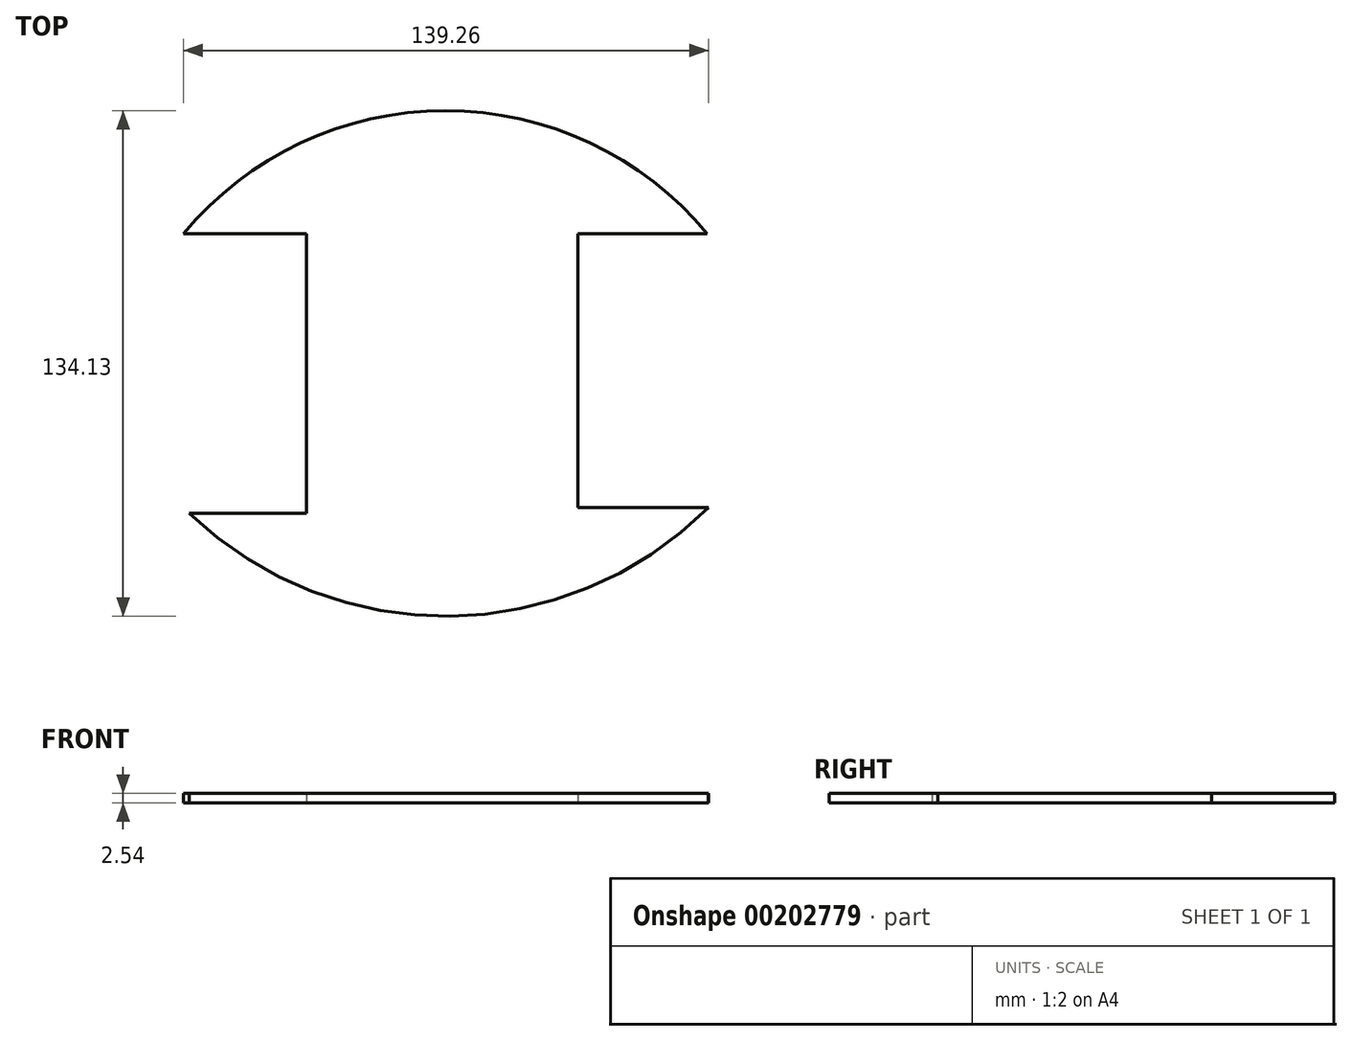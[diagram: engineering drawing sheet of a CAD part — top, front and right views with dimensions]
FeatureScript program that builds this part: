
annotation { "Feature Type Name" : "Feature", "Feature Type Description" : "" }
export const myFeature = defineFeature(function(context is Context, id is Id, definition is map)
    precondition{}
    {
        {
            var Q0;
            Q0=qCreatedBy(makeId("Top.planeOp"),FACE);
            var sketch = newSketch(context, id + "F0", { "sketchPlane" : qUnion([Q0])});
            skPoint(sketch, "E0.end.orphan", {"position": v(-38.72, 11.16) * mm});
            skPoint(sketch, "E1.start.orphan", {"position": v(-30.7, -21.46) * mm});
            skPoint(sketch, "E2.start.orphan", {"position": v(-38.72, -21.46) * mm});
            skPoint(sketch, "E3.end.orphan", {"position": v(21.74, -21.46) * mm});
            skPoint(sketch, "E4.start.orphan", {"position": v(21.74, 11.16) * mm});
            skLineSegment(sketch, "E5", {"start": v(-36.62, 25.84) * mm, "end": v(-36.62, -48.35) * mm});
            skLineSegment(sketch, "E6", {"start": v(-36.62, 25.84) * mm, "end": v(-69.19, 25.84) * mm});
            skLineSegment(sketch, "E7", {"start": v(35.48, 25.84) * mm, "end": v(35.48, -46.82) * mm});
            skLineSegment(sketch, "E8", {"start": v(35.48, 25.84) * mm, "end": v(69.76, 25.84) * mm});
            skLineSegment(sketch, "E9", {"start": v(35.48, -46.82) * mm, "end": v(70.07, -46.82) * mm});
            skLineSegment(sketch, "E10", {"start": v(-36.62, -48.35) * mm, "end": v(-67.68, -48.35) * mm});
            skPoint(sketch, "E11.orphan", {"position": v(31.85, -46.82) * mm});
            skArc(sketch, "E12", {"start": v(69.76, 25.84) * mm, "mid": v(0.29, 58.48) * mm, "end": v(-69.19, 25.84) * mm});
            skArc(sketch, "E13", {"start": v(-67.68, -48.35) * mm, "mid": v(1.5, -75.64) * mm, "end": v(70.07, -46.82) * mm});
            skSolve(sketch);
        }
        {
            var Q0;
            Q0=makeQuery(id+"F0.imprint","IMPRINT",FACE,{"disambiguationData":[TD([[makeQuery(id+"F0.imprint","IMPRINT",EDGE,{"derivedFrom":sQuery(id+"F0.wireOp",EDGE,"E5")}),1.0]])]});
            extrude(context, id + "F1", {"entities" : qUnion([Q0]), "depth" : 2.54 * mm});
        }
    });
